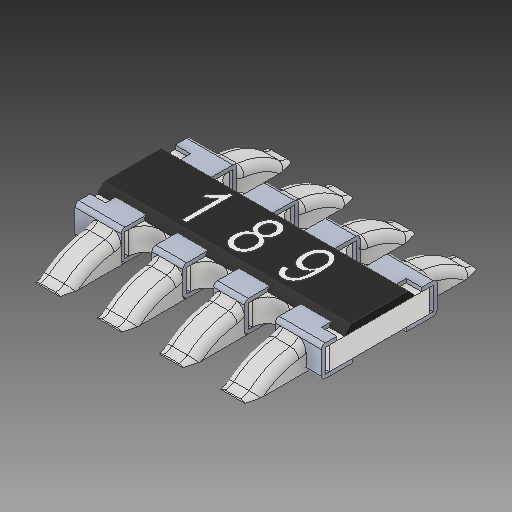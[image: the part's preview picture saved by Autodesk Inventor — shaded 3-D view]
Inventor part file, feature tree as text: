
AUTODESK INVENTOR PART (.ipt)
format: ipt  version: 2019.4 (Build 234330000, 330)  size: 609,280 bytes
history: native  units: mm
features: other x8, fillet x2
ambient origin geometry x8: Origin, YZ Plane, XZ Plane, XY Plane, X Axis, Y Axis, Z Axis, Center Point
bodies: Solid1 (feature_tree), Solid2 (feature_tree), Solid3 (feature_tree), Solid4 (feature_tree), Solid5 (feature_tree), Solid6 (feature_tree), Solid7 (feature_tree), Solid8 (feature_tree), Solid9 (feature_tree), Solid10 (feature_tree)
feature tree (10):
  other  "Cut-Extrude7"
  other  "Boss-Extrude5"
  fillet  "Fillet2"  [1 undecoded]
  fillet  "Fillet1"  [1 undecoded]
  other  "LPattern3[1]"
  other  "LPattern3[2]"
  other  "LPattern3[3]"
  other  "LPattern3[4]"
  other  "LPattern3[5]"
  other  "LPattern3[6]"
note: 2 required parameter values undecoded (feature->parameter linkage not recoverable at this tier; creation-order binding heuristic only, values carry confidence <= 0.55)
